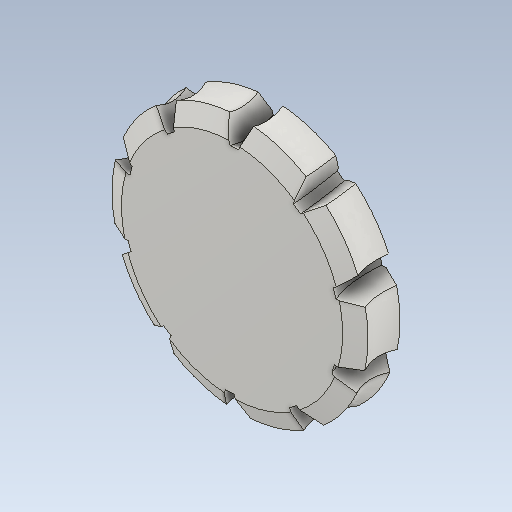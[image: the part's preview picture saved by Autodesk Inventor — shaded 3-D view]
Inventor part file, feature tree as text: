
AUTODESK INVENTOR PART (.ipt)
format: ipt  version: 2021 (Build 250183000, 183)  size: 311,808 bytes
history: native  units: mm (DEFAULTED — no unit token found)
features: other x8, plane x3, pattern_circular x1, sketch x1
ambient origin geometry x5: Origin, X Axis, Y Axis, Z Axis, Center Point
bodies: Solid1 (feature_tree)
feature tree (13):
  other  "Tooth Plane"
  other  "Base Body Sketch"
  other  "Base Body"
  other  "Base Body2"
  plane  "Work Plane13"
  other  "Tooth"
  pattern_circular  "Tooth Pattern"  [2 undecoded]
  plane  "Work Plane14"
  plane  "Work Plane15"
  other  "Tooth Sketch"
  sketch  "Sketch8"  dims[d35=90.0deg d37=-0.996687mm d38=68.0168mm d39=3.490659mm d40=14.6mm d41=20.0mm d42=3.769911mm d43=90.0deg d44=100.0mm d46=360.0deg d50=4.297754mm d68=68.0168mm d69=0.0mm d73=0.0mm d75=3.141593mm d77=96.0mm d78=20.0mm d79=0.0mm d80=0.0mm d81=0.0mm d82=0.0mm d83=3.141593mm d84=0.0mm d85=180.0deg d86=68.0168mm d87=108.0336mm d89=32.0mm d90=90.0deg d92=20.0mm d93=68.0168mm]
  other  "Srf1"
  other  "Pitch Diameter"
note: 2 required parameter values undecoded (feature->parameter linkage not recoverable at this tier; creation-order binding heuristic only, values carry confidence <= 0.55)
